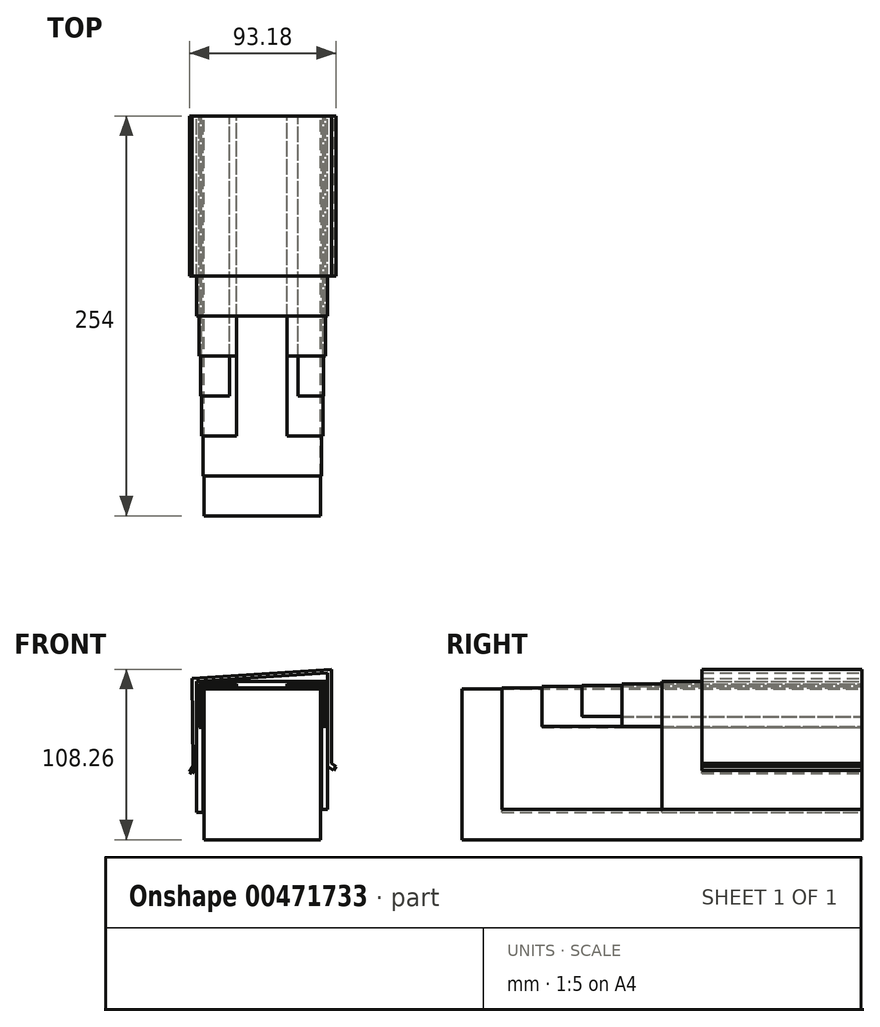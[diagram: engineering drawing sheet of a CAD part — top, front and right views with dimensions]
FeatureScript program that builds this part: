
annotation { "Feature Type Name" : "Feature", "Feature Type Description" : "" }
export const myFeature = defineFeature(function(context is Context, id is Id, definition is map)
    precondition{}
    {
        {
            var Q0;
            Q0=qCreatedBy(makeId("Front.planeOp"),FACE);
            var sketch = newSketch(context, id + "F0", { "sketchPlane" : qUnion([Q0])});
            skLineSegment(sketch, "E0.bottom", {"start": v(-44.3, -53.92) * mm, "end": v(29.75, -53.92) * mm});
            skLineSegment(sketch, "E0.top", {"start": v(-44.3, 41.87) * mm, "end": v(29.75, 41.87) * mm});
            skLineSegment(sketch, "E0.left", {"start": v(-44.3, -53.92) * mm, "end": v(-44.3, 41.87) * mm});
            skLineSegment(sketch, "E0.right", {"start": v(29.75, -53.92) * mm, "end": v(29.75, 41.87) * mm});
            skLineSegment(sketch, "E1", {"start": v(-44.3, -36.74) * mm, "end": v(-44.8, -36.74) * mm});
            skLineSegment(sketch, "E2", {"start": v(-44.8, -36.74) * mm, "end": v(-44.8, 42.38) * mm});
            skLineSegment(sketch, "E3", {"start": v(-44.8, 42.38) * mm, "end": v(30.26, 42.38) * mm});
            skLineSegment(sketch, "E4", {"start": v(30.26, 42.38) * mm, "end": v(30.26, -34.78) * mm});
            skLineSegment(sketch, "E5", {"start": v(30.26, -34.78) * mm, "end": v(29.75, -34.78) * mm});
            skLineSegment(sketch, "E6", {"start": v(29.75, 41.87) * mm, "end": v(30.26, 41.87) * mm, "construction": true});
            skLineSegment(sketch, "E7", {"start": v(-44.3, 41.87) * mm, "end": v(-44.8, 41.87) * mm, "construction": true});
            skLineSegment(sketch, "E8", {"start": v(-44.8, 17.49) * mm, "end": v(-45.82, 17.49) * mm});
            skLineSegment(sketch, "E9", {"start": v(-45.82, 17.49) * mm, "end": v(-45.82, 43.4) * mm});
            skLineSegment(sketch, "E10", {"start": v(-45.82, 43.4) * mm, "end": v(-23.62, 43.4) * mm});
            skLineSegment(sketch, "E11", {"start": v(-23.62, 43.4) * mm, "end": v(-23.62, 42.38) * mm});
            skLineSegment(sketch, "E12", {"start": v(-45.82, 24.06) * mm, "end": v(-46.33, 24.06) * mm});
            skLineSegment(sketch, "E13", {"start": v(-46.33, 24.06) * mm, "end": v(-46.33, 43.9) * mm});
            skLineSegment(sketch, "E14", {"start": v(-46.33, 43.9) * mm, "end": v(-27.95, 43.9) * mm});
            skLineSegment(sketch, "E15", {"start": v(-27.95, 43.9) * mm, "end": v(-27.95, 43.4) * mm});
            skLineSegment(sketch, "E16", {"start": v(-45.82, 17.49) * mm, "end": v(-47.35, 17.49) * mm});
            skLineSegment(sketch, "E17", {"start": v(-47.35, 17.49) * mm, "end": v(-47.35, 44.92) * mm});
            skLineSegment(sketch, "E18", {"start": v(-47.35, 44.92) * mm, "end": v(-23.62, 44.92) * mm});
            skLineSegment(sketch, "E19", {"start": v(-23.62, 44.92) * mm, "end": v(-23.62, 43.4) * mm});
            skLineSegment(sketch, "E20", {"start": v(8.32, 42.38) * mm, "end": v(8.32, 43.4) * mm});
            skLineSegment(sketch, "E21", {"start": v(8.32, 43.4) * mm, "end": v(31.27, 43.4) * mm});
            skLineSegment(sketch, "E22", {"start": v(31.27, 43.4) * mm, "end": v(31.27, 18.12) * mm});
            skLineSegment(sketch, "E23", {"start": v(31.27, 18.12) * mm, "end": v(30.26, 18.12) * mm});
            skLineSegment(sketch, "E24", {"start": v(15.35, 43.4) * mm, "end": v(15.35, 43.9) * mm});
            skLineSegment(sketch, "E25", {"start": v(15.35, 43.9) * mm, "end": v(31.78, 43.9) * mm});
            skLineSegment(sketch, "E26", {"start": v(31.78, 43.9) * mm, "end": v(31.78, 24.27) * mm});
            skLineSegment(sketch, "E27", {"start": v(31.78, 24.27) * mm, "end": v(31.27, 24.27) * mm});
            skLineSegment(sketch, "E28", {"start": v(8.32, 43.4) * mm, "end": v(8.32, 44.92) * mm});
            skLineSegment(sketch, "E29", {"start": v(8.32, 44.92) * mm, "end": v(32.8, 44.92) * mm});
            skLineSegment(sketch, "E30", {"start": v(32.8, 44.92) * mm, "end": v(32.8, 18.12) * mm});
            skLineSegment(sketch, "E31", {"start": v(32.8, 18.12) * mm, "end": v(31.27, 18.12) * mm});
            skLineSegment(sketch, "E32", {"start": v(-44.8, -36.74) * mm, "end": v(-48.87, -36.74) * mm});
            skLineSegment(sketch, "E33", {"start": v(-48.87, -36.74) * mm, "end": v(-48.87, 46.45) * mm});
            skLineSegment(sketch, "E34", {"start": v(-48.87, 46.45) * mm, "end": v(34.32, 46.45) * mm});
            skLineSegment(sketch, "E35", {"start": v(34.32, 46.45) * mm, "end": v(34.32, -34.82) * mm});
            skLineSegment(sketch, "E36", {"start": v(34.32, -34.82) * mm, "end": v(30.26, -34.78) * mm});
            skLineSegment(sketch, "E37", {"start": v(-7.28, 46.45) * mm, "end": v(-7.28, 42.38) * mm, "construction": true});
            skLineSegment(sketch, "E38", {"start": v(-48.87, -7.43) * mm, "end": v(-51.91, -11.98) * mm});
            skLineSegment(sketch, "E39", {"start": v(-51.91, -11.98) * mm, "end": v(-53.54, -10.9) * mm});
            skLineSegment(sketch, "E40", {"start": v(-53.54, -10.9) * mm, "end": v(-51.26, -7.5) * mm});
            skLineSegment(sketch, "E41", {"start": v(-51.26, -7.5) * mm, "end": v(-51.91, 48.55) * mm});
            skLineSegment(sketch, "E42", {"start": v(-51.91, 48.55) * mm, "end": v(36.74, 54.34) * mm});
            skLineSegment(sketch, "E43", {"start": v(36.74, 54.34) * mm, "end": v(36.74, -5.5) * mm});
            skLineSegment(sketch, "E44", {"start": v(36.74, -5.5) * mm, "end": v(39.64, -7.5) * mm});
            skLineSegment(sketch, "E45", {"start": v(39.64, -7.5) * mm, "end": v(37.9, -10) * mm});
            skLineSegment(sketch, "E46", {"start": v(37.9, -10) * mm, "end": v(34.27, -7.5) * mm});
            skLineSegment(sketch, "E47", {"start": v(34.32, 46.45) * mm, "end": v(34.32, 51.86) * mm});
            skLineSegment(sketch, "E48", {"start": v(34.32, 51.86) * mm, "end": v(-48.87, 46.45) * mm});
            skSolve(sketch);
        }
        {
            var Q0;
            {var subQ3=sQuery(id+"F0.wireOp",EDGE,"E0.bottom");Q0=makeQuery(id+"F0.imprint","IMPRINT",FACE,{"disambiguationData":[TD([[makeQuery(id+"F0.imprint","IMPRINT",EDGE,{"derivedFrom":subQ3}),1.0]])]});}
            extrude(context, id + "F1", {"entities" : qUnion([Q0]), "depth" : 254 * mm});
        }
        {
            var Q0;
            {var subQ10=sQuery(id+"F0.wireOp",EDGE,"E0.top");Q0=makeQuery(id+"F0.imprint","IMPRINT",FACE,{"disambiguationData":[TD([[makeQuery(id+"F0.imprint","IMPRINT",EDGE,{"derivedFrom":subQ10}),1.0]])]});}
            extrude(context, id + "F2", {"entities" : qUnion([Q0]), "depth" : 228.6 * mm});
        }
        {
            var Q0;
            {var subQ1=sQuery(id+"F0.wireOp",EDGE,"E8");Q0=makeQuery(id+"F0.imprint","IMPRINT",FACE,{"disambiguationData":[TD([[makeQuery(id+"F0.imprint","IMPRINT",EDGE,{"derivedFrom":subQ1}),-1.0]])]});}
            extrude(context, id + "F3", {"entities" : qUnion([Q0]), "depth" : 203.2 * mm});
        }
        {
            var Q0;
            {var subQ0=sQuery(id+"F0.wireOp",EDGE,"E12");Q0=makeQuery(id+"F0.imprint","IMPRINT",FACE,{"disambiguationData":[TD([[makeQuery(id+"F0.imprint","IMPRINT",EDGE,{"derivedFrom":subQ0}),-1.0]])]});}
            extrude(context, id + "F4", {"entities" : qUnion([Q0]), "depth" : 177.8 * mm});
        }
        {
            var Q0;
            {var subQ3=sQuery(id+"F0.wireOp",EDGE,"E12");Q0=makeQuery(id+"F0.imprint","IMPRINT",FACE,{"disambiguationData":[TD([[makeQuery(id+"F0.imprint","IMPRINT",EDGE,{"derivedFrom":subQ3}),1.0]])]});}
            extrude(context, id + "F5", {"entities" : qUnion([Q0]), "depth" : 152.4 * mm});
        }
        {
            var Q0;
            {var subQ1=sQuery(id+"F0.wireOp",EDGE,"E20");Q0=makeQuery(id+"F0.imprint","IMPRINT",FACE,{"disambiguationData":[TD([[makeQuery(id+"F0.imprint","IMPRINT",EDGE,{"derivedFrom":subQ1}),-1.0]])]});}
            extrude(context, id + "F6", {"entities" : qUnion([Q0]), "depth" : 203.2 * mm});
        }
        {
            var Q0;
            {var subQ0=sQuery(id+"F0.wireOp",EDGE,"E24");Q0=makeQuery(id+"F0.imprint","IMPRINT",FACE,{"disambiguationData":[TD([[makeQuery(id+"F0.imprint","IMPRINT",EDGE,{"derivedFrom":subQ0}),-1.0]])]});}
            extrude(context, id + "F7", {"entities" : qUnion([Q0]), "depth" : 177.8 * mm});
        }
        {
            var Q0;
            {var subQ3=sQuery(id+"F0.wireOp",EDGE,"E24");Q0=makeQuery(id+"F0.imprint","IMPRINT",FACE,{"disambiguationData":[TD([[makeQuery(id+"F0.imprint","IMPRINT",EDGE,{"derivedFrom":subQ3}),1.0]])]});}
            extrude(context, id + "F8", {"entities" : qUnion([Q0]), "depth" : 152.4 * mm});
        }
        {
            var Q0;
            {var subQ7=sQuery(id+"F0.wireOp",EDGE,"E8");Q0=makeQuery(id+"F0.imprint","IMPRINT",FACE,{"disambiguationData":[TD([[makeQuery(id+"F0.imprint","IMPRINT",EDGE,{"derivedFrom":subQ7}),1.0]])]});}
            extrude(context, id + "F9", {"entities" : qUnion([Q0]), "depth" : 127 * mm});
        }
        {
            var Q0;
            {var subQ4=sQuery(id+"F0.wireOp",EDGE,"E38");Q0=makeQuery(id+"F0.imprint","IMPRINT",FACE,{"disambiguationData":[TD([[makeQuery(id+"F0.imprint","IMPRINT",EDGE,{"derivedFrom":subQ4}),-1.0]])]});}
            extrude(context, id + "F10", {"entities" : qUnion([Q0]), "depth" : 101.6 * mm});
        }
    });
